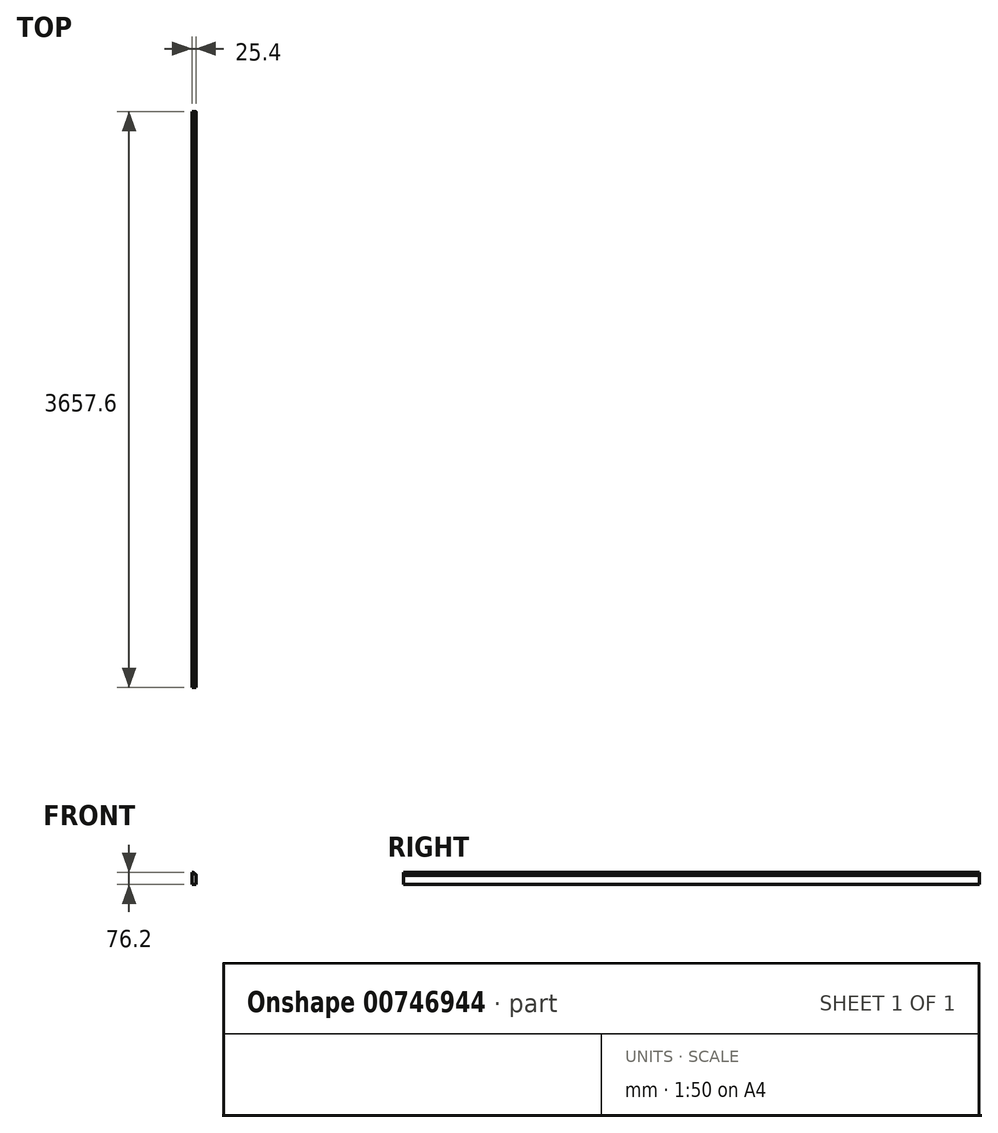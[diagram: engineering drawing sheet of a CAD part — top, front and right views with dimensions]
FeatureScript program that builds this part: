
annotation { "Feature Type Name" : "Feature", "Feature Type Description" : "" }
export const myFeature = defineFeature(function(context is Context, id is Id, definition is map)
    precondition{}
    {
        {
            var Q0;
            Q0=qCreatedBy(makeId("Front.planeOp"),FACE);
            var sketch = newSketch(context, id + "F0", { "sketchPlane" : qUnion([Q0])});
            skLineSegment(sketch, "E0", {"start": v(25.4, 0) * mm, "end": v(0, 0) * mm});
            skLineSegment(sketch, "E1", {"start": v(25.4, 58.16) * mm, "end": v(25.4, 0) * mm});
            skLineSegment(sketch, "E2", {"start": v(0, 76.2) * mm, "end": v(0, 0) * mm});
            skLineSegment(sketch, "E3", {"start": v(0, 76.2) * mm, "end": v(10.5, 76.2) * mm});
            skLineSegment(sketch, "E4", {"start": v(10.5, 76.2) * mm, "end": v(10.5, 74.48) * mm});
            skArc(sketch, "E5", {"start": v(16.43, 69.97) * mm, "mid": v(14.2, 73.2) * mm, "end": v(10.5, 74.48) * mm});
            skArc(sketch, "E6", {"start": v(16.43, 69.97) * mm, "mid": v(18.68, 67.68) * mm, "end": v(21.77, 66.8) * mm});
            skLineSegment(sketch, "E7", {"start": v(21.77, 66.8) * mm, "end": v(21.78, 65.53) * mm});
            skArc(sketch, "E8", {"start": v(21.37, 58.59) * mm, "mid": v(25.27, 61.84) * mm, "end": v(21.78, 65.53) * mm});
            skLineSegment(sketch, "E9", {"start": v(21.37, 58.59) * mm, "end": v(21.36, 58.16) * mm});
            skLineSegment(sketch, "E10", {"start": v(21.36, 58.16) * mm, "end": v(25.4, 58.16) * mm});
            skSolve(sketch);
        }
        {
            var Q0;
            Q0=makeQuery(id+"F0.imprint","IMPRINT",FACE,{"disambiguationData":[TD([[makeQuery(id+"F0.imprint","IMPRINT",EDGE,{"derivedFrom":sQuery(id+"F0.wireOp",EDGE,"E0")}),-1.0]])]});
            extrude(context, id + "F1", {"entities" : qUnion([Q0]), "depth" : 1828.8 * mm, "offsetDistance" : 25.4 * mm, "hasSecondDirection" : true, "secondDirectionOppositeDirection" : true, "secondDirectionDepth" : 1828.8 * mm});
        }
    });
